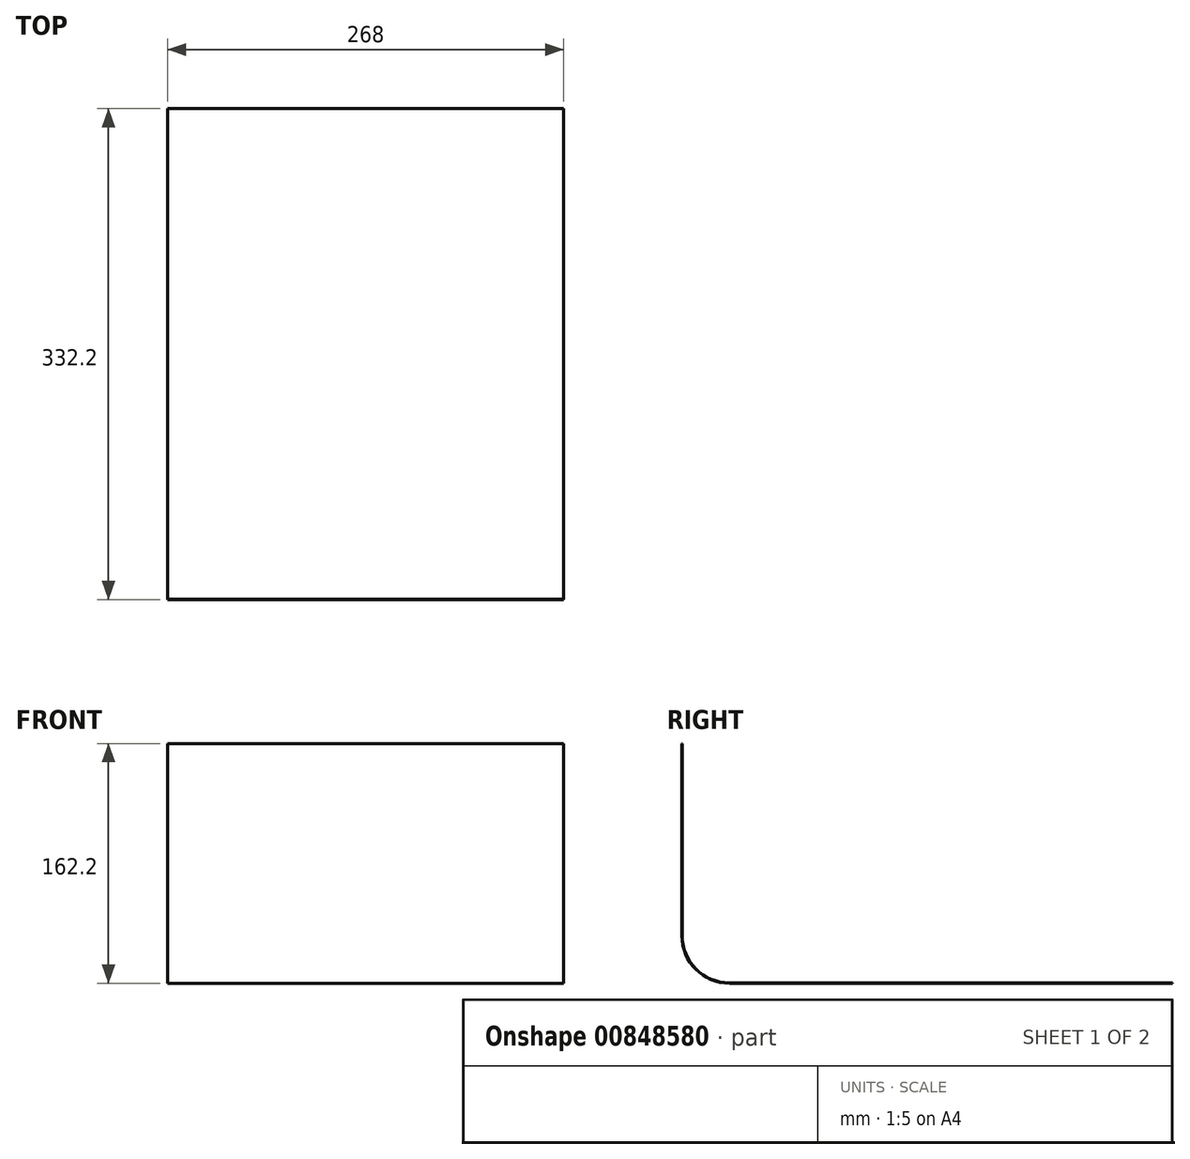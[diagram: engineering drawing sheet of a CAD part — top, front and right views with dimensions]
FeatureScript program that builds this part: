
annotation { "Feature Type Name" : "Feature", "Feature Type Description" : "" }
export const myFeature = defineFeature(function(context is Context, id is Id, definition is map)
    precondition{}
    {
        {
            var Q0;
            Q0=qCreatedBy(makeId("Right.planeOp"),FACE);
            var sketch = newSketch(context, id + "F0", { "sketchPlane" : qUnion([Q0])});
            skLineSegment(sketch, "E0", {"start": v(0, 0) * mm, "end": v(32, 0) * mm, "construction": true});
            skLineSegment(sketch, "E1", {"start": v(0, 0) * mm, "end": v(0, 32) * mm, "construction": true});
            skArc(sketch, "E2", {"start": v(0, 32) * mm, "mid": v(9.37, 9.37) * mm, "end": v(32, 0) * mm});
            skLineSegment(sketch, "E3", {"start": v(32, 0) * mm, "end": v(332, 0) * mm});
            skLineSegment(sketch, "E4", {"start": v(0, 32) * mm, "end": v(0, 162) * mm});
            skLineSegment(sketch, "E5.0", {"start": v(-0.2, 32) * mm, "end": v(-0.2, 162) * mm});
            skArc(sketch, "E5.1", {"start": v(-0.2, 32) * mm, "mid": v(9.23, 9.23) * mm, "end": v(32, -0.2) * mm});
            skLineSegment(sketch, "E5.2", {"start": v(32, -0.2) * mm, "end": v(332, -0.2) * mm});
            skLineSegment(sketch, "E6", {"start": v(-0.2, 162) * mm, "end": v(0, 162) * mm});
            skLineSegment(sketch, "E7", {"start": v(332, 0) * mm, "end": v(332, -0.2) * mm});
            skLineSegment(sketch, "E8", {"start": v(132.1, 0) * mm, "end": v(132.1, 52.75) * mm, "construction": true});
            skSolve(sketch);
        }
        {
            var Q0;
            Q0 = qSketchRegion(id + "F0", true);
            extrude(context, id + "F1", {"entities" : qUnion([Q0]), "depth" : 268 * mm, "offsetDistance" : 25 * mm});
        }
    });
